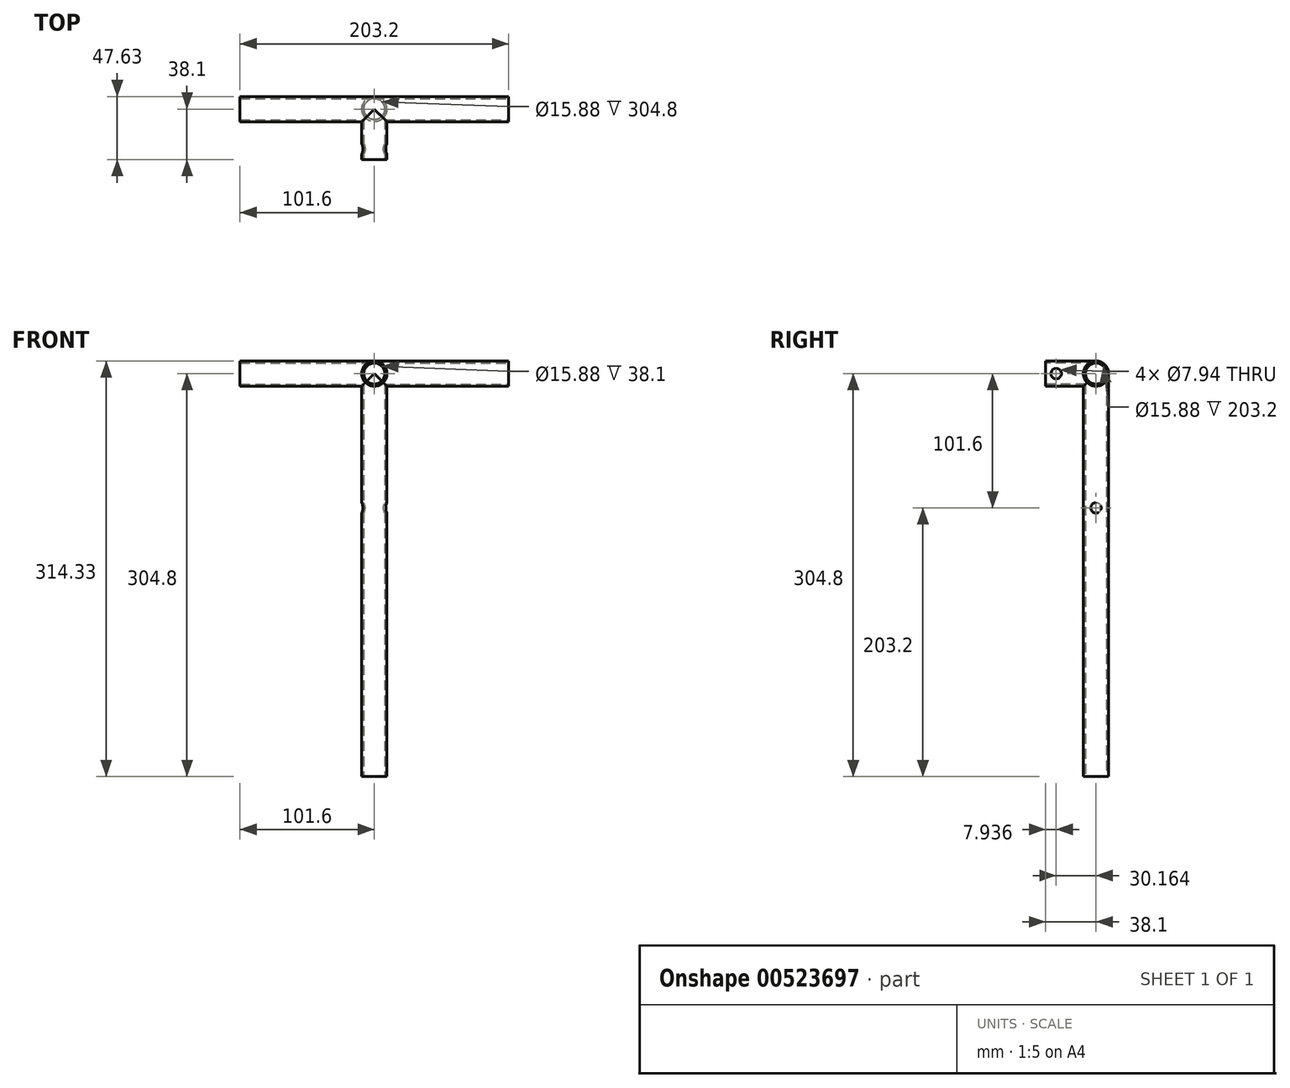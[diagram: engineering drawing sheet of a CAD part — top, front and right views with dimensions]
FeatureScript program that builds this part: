
annotation { "Feature Type Name" : "Feature", "Feature Type Description" : "" }
export const myFeature = defineFeature(function(context is Context, id is Id, definition is map)
    precondition{}
    {
        {
            var Q0;
            Q0=qCreatedBy(makeId("Right.planeOp"),FACE);
            var sketch = newSketch(context, id + "F0", { "sketchPlane" : qUnion([Q0])});
            skCircle(sketch, "E0", {"center": v(0, 0) * mm, "radius": 9.53 * mm});
            skSolve(sketch);
        }
        {
            var Q0;
            Q0=makeQuery(id+"F0.imprint","IMPRINT",FACE,{"disambiguationData":[TD([[makeQuery(id+"F0.imprint","IMPRINT",EDGE,{"derivedFrom":sQuery(id+"F0.wireOp",EDGE,"E0")}),1.0]])]});
            extrude(context, id + "F1", {"entities" : qUnion([Q0]), "depth" : 101.6 * mm, "offsetDistance" : 25.4 * mm});
        }
        {
            var Q0;
            Q0=makeQuery(id+"F1.opExtrude","CAP_FACE",FACE,{"disambiguationData":[OSD([sQuery(id+"F0.wireOp",EDGE,"E0")])],"isStart":true});
            extrude(context, id + "F2", {"entities" : qUnion([Q0]), "operationType" : NewBodyOperationType.ADD, "depth" : 101.6 * mm, "offsetDistance" : 25.4 * mm});
        }
        {
            var Q0;
            Q0=qCreatedBy(makeId("Top.planeOp"),FACE);
            var sketch = newSketch(context, id + "F3", { "sketchPlane" : qUnion([Q0])});
            skCircle(sketch, "E1", {"center": v(0, 0) * mm, "radius": 9.52 * mm});
            skSolve(sketch);
        }
        {
            var Q0;
            Q0 = qSketchRegion(id + "F3", true);
            var Q1;
            Q1=sQuery(id+"F3.wireOp",EDGE,"E1");
            extrude(context, id + "F4", {"entities" : qUnion([Q0]), "operationType" : NewBodyOperationType.ADD, "surfaceEntities" : qUnion([Q1]), "oppositeDirection" : true, "depth" : 304.8 * mm, "offsetDistance" : 25.4 * mm});
        }
        {
            var Q0;
            Q0=qCreatedBy(makeId("Front.planeOp"),FACE);
            var sketch = newSketch(context, id + "F5", { "sketchPlane" : qUnion([Q0])});
            skCircle(sketch, "E2", {"center": v(0, 0) * mm, "radius": 9.53 * mm});
            skSolve(sketch);
        }
        {
            var Q0;
            Q0=makeQuery(id+"F5.imprint","IMPRINT",FACE,{"disambiguationData":[TD([[makeQuery(id+"F5.imprint","IMPRINT",EDGE,{"derivedFrom":sQuery(id+"F5.wireOp",EDGE,"E2")}),1.0]])]});
            var Q1;
            Q1=sQuery(id+"F5.wireOp",EDGE,"E2");
            extrude(context, id + "F6", {"entities" : qUnion([Q0]), "operationType" : NewBodyOperationType.ADD, "surfaceEntities" : qUnion([Q1]), "depth" : 38.1 * mm, "offsetDistance" : 25.4 * mm});
        }
        {
            var Q0;
            Q0=qCreatedBy(makeId("Right.planeOp"),FACE);
            var sketch = newSketch(context, id + "F7", { "sketchPlane" : qUnion([Q0])});
            skCircle(sketch, "E3", {"center": v(-30.16, 0) * mm, "radius": 3.97 * mm});
            skLineSegment(sketch, "E4", {"start": v(-38.1, 0) * mm, "end": v(-30.16, 0) * mm, "construction": true});
            skSolve(sketch);
        }
        {
            var Q0;
            Q0 = qSketchRegion(id + "F7", true);
            var Q1;
            Q1=sQuery(id+"F7.wireOp",EDGE,"E3");
            extrude(context, id + "F8", {"entities" : qUnion([Q0]), "operationType" : NewBodyOperationType.REMOVE, "surfaceEntities" : qUnion([Q1]), "endBound" : BoundingType.THROUGH_ALL, "oppositeDirection" : true, "depth" : 25.4 * mm, "offsetDistance" : 25.4 * mm, "hasSecondDirection" : true, "secondDirectionBound" : SecondDirectionBoundingType.THROUGH_ALL, "secondDirectionOppositeDirection" : false, "secondDirectionDepth" : -25.4 * mm});
        }
        {
            var Q0;
            Q0=makeQuery(id+"F1.opExtrude","CAP_FACE",FACE,{"disambiguationData":[OSD([sQuery(id+"F0.wireOp",EDGE,"E0")])],"isStart":false});
            var sketch = newSketch(context, id + "F9", { "sketchPlane" : qUnion([Q0])});
            skCircle(sketch, "E5", {"center": v(0, 0) * mm, "radius": 7.94 * mm});
            skSolve(sketch);
        }
        {
            var Q0;
            Q0=makeQuery(id+"F9.imprint","IMPRINT",FACE,{"disambiguationData":[TD([[makeQuery(id+"F9.imprint","IMPRINT",EDGE,{"derivedFrom":sQuery(id+"F9.wireOp",EDGE,"E5")}),1.0]])]});
            var Q1;
            Q1=sQuery(id+"F9.wireOp",EDGE,"E5");
            extrude(context, id + "F10", {"entities" : qUnion([Q0]), "operationType" : NewBodyOperationType.REMOVE, "surfaceEntities" : qUnion([Q1]), "endBound" : BoundingType.THROUGH_ALL, "oppositeDirection" : true, "depth" : 25.4 * mm, "offsetDistance" : 25.4 * mm});
        }
        {
            var Q0;
            Q0=makeQuery(id+"F6.opExtrude","CAP_FACE",FACE,{"disambiguationData":[OSD([sQuery(id+"F5.wireOp",EDGE,"E2")])],"isStart":false});
            var sketch = newSketch(context, id + "F11", { "sketchPlane" : qUnion([Q0])});
            skCircle(sketch, "E6", {"center": v(0, 0) * mm, "radius": 7.94 * mm});
            skSolve(sketch);
        }
        {
            var Q0;
            Q0=makeQuery(id+"F11.imprint","IMPRINT",FACE,{"disambiguationData":[TD([[makeQuery(id+"F11.imprint","IMPRINT",EDGE,{"derivedFrom":sQuery(id+"F11.wireOp",EDGE,"E6")}),1.0]])]});
            var Q1;
            Q1=makeQuery(id+"F1.opExtrude","SWEPT_BODY",BODY,{"disambiguationData":[OSD([sQuery(id+"F0.wireOp",EDGE,"E0")])]});
            extrude(context, id + "F12", {"entities" : qUnion([Q0]), "operationType" : NewBodyOperationType.REMOVE, "endBound" : BoundingType.UP_TO_BODY, "oppositeDirection" : true, "depth" : 25.4 * mm, "endBoundEntityBody" : qUnion([Q1]), "offsetDistance" : 25.4 * mm});
        }
        {
            var Q0;
            Q0=makeQuery(id+"F4.opExtrude","CAP_FACE",FACE,{"disambiguationData":[OSD([sQuery(id+"F3.wireOp",EDGE,"E1")])],"isStart":false});
            var sketch = newSketch(context, id + "F13", { "sketchPlane" : qUnion([Q0])});
            skCircle(sketch, "E7", {"center": v(0, 0) * mm, "radius": 7.94 * mm});
            skSolve(sketch);
        }
        {
            var Q0;
            Q0=makeQuery(id+"F13.imprint","IMPRINT",FACE,{"disambiguationData":[TD([[makeQuery(id+"F13.imprint","IMPRINT",EDGE,{"derivedFrom":sQuery(id+"F13.wireOp",EDGE,"E7")}),1.0]])]});
            var Q1;
            Q1=makeQuery(id+"F1.opExtrude","SWEPT_BODY",BODY,{"disambiguationData":[OSD([sQuery(id+"F0.wireOp",EDGE,"E0")])]});
            extrude(context, id + "F14", {"entities" : qUnion([Q0]), "operationType" : NewBodyOperationType.REMOVE, "endBound" : BoundingType.UP_TO_BODY, "oppositeDirection" : true, "depth" : 25.4 * mm, "endBoundEntityBody" : qUnion([Q1]), "offsetDistance" : 25.4 * mm});
        }
        {
            var Q0;
            Q0=qCreatedBy(makeId("Right.planeOp"),FACE);
            var sketch = newSketch(context, id + "F15", { "sketchPlane" : qUnion([Q0])});
            skCircle(sketch, "E8", {"center": v(0, -101.6) * mm, "radius": 3.97 * mm});
            skLineSegment(sketch, "E9", {"start": v(0, 0) * mm, "end": v(0, -101.6) * mm, "construction": true});
            skSolve(sketch);
        }
        {
            var Q0;
            Q0 = qSketchRegion(id + "F15", true);
            extrude(context, id + "F16", {"entities" : qUnion([Q0]), "operationType" : NewBodyOperationType.REMOVE, "endBound" : BoundingType.THROUGH_ALL, "oppositeDirection" : true, "depth" : 25.4 * mm, "offsetDistance" : 25.4 * mm, "hasSecondDirection" : true, "secondDirectionBound" : SecondDirectionBoundingType.THROUGH_ALL, "secondDirectionOppositeDirection" : false, "secondDirectionDepth" : 25.4 * mm});
        }
    });
